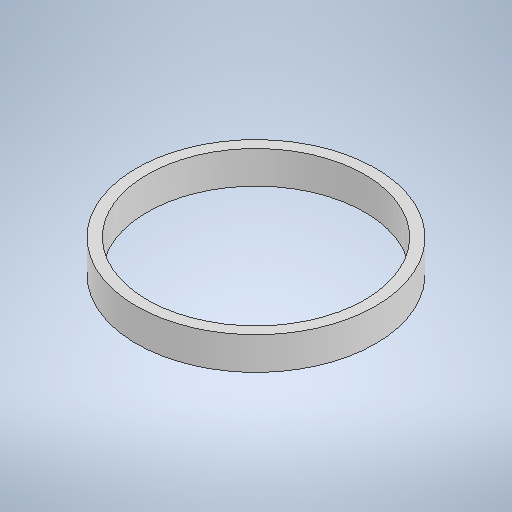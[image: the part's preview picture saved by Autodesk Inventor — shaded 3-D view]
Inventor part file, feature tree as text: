
AUTODESK INVENTOR PART (.ipt)
format: ipt  version: 2025.1 (Build 291241000, 241)  size: 243,200 bytes
history: native  units: mm
features: extrude x1, sketch x1
ambient origin geometry x8: Origin, YZ Plane, XZ Plane, XY Plane, X Axis, Y Axis, Z Axis, Center Point
bodies: Solid1 (feature_tree)
feature tree (2):
  extrude  "Extrusion1"  Depth=3.0mm
  sketch  "Sketch1"  dims[d0=22.0mm d1=20.0mm d2=3.0mm d3=0.0mm]
